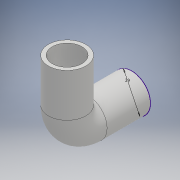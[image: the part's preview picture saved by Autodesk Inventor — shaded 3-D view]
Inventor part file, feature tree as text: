
AUTODESK INVENTOR PART (.ipt)
format: ipt  version: 2017 (Build 210142000, 142)  size: 151,040 bytes
history: native  units: mm
features: sketch x3, plane x2, sweep x1, shell x1
ambient origin geometry x8: Origin, YZ Plane, XZ Plane, XY Plane, X Axis, Y Axis, Z Axis, Center Point
bodies: Solid1 (feature_tree)
feature tree (7):
  plane  "Work Plane1"
  sketch  "Sketch1"  dims[d0=50.0mm d1=29.0mm d2=50.0mm]
  plane  "Work Plane2"
  sketch  "Sketch2"  dims[d3=29.0mm]
  sweep  "Sweep1"
  shell  "Shell1"  Thickness=50.0mm
  sketch  "Sketch3"  dims[d4=2.0mm d5=0.0mm d6=0.0mm d7=3.0mm]
